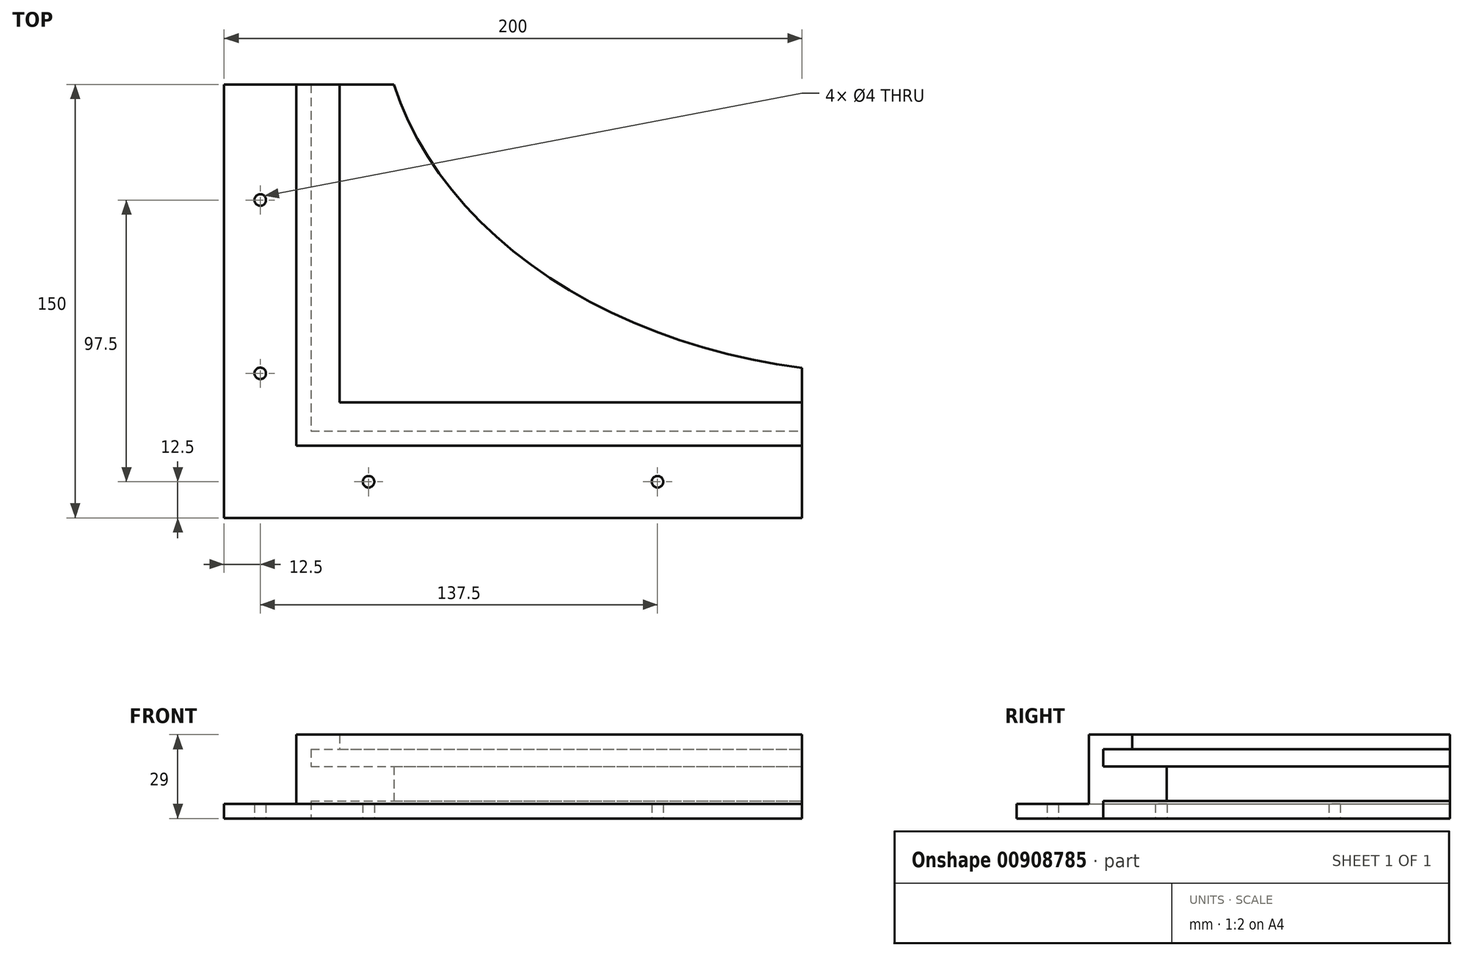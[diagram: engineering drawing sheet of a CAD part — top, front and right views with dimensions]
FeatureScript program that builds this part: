
annotation { "Feature Type Name" : "Feature", "Feature Type Description" : "" }
export const myFeature = defineFeature(function(context is Context, id is Id, definition is map)
    precondition{}
    {
        {
            var Q0;
            Q0=qCreatedBy(makeId("Top.planeOp"),FACE);
            var sketch = newSketch(context, id + "F0", { "sketchPlane" : qUnion([Q0])});
            skEllipticalArc(sketch, "E0", {});
            skLineSegment(sketch, "E1", {"start": v(-176, 0) * mm, "end": v(-176, -130) * mm});
            skPoint(sketch, "E1.endSnap0", {"position": v(0, -130) * mm});
            skLineSegment(sketch, "E2", {"start": v(-176, -130) * mm, "end": v(0, -130) * mm});
            skLineSegment(sketch, "E3", {"start": v(-176, 0) * mm, "end": v(-200, 0) * mm});
            skLineSegment(sketch, "E4", {"start": v(-200, 0) * mm, "end": v(-200, -150) * mm});
            skLineSegment(sketch, "E5", {"start": v(-200, -150) * mm, "end": v(0, -150) * mm});
            skLineSegment(sketch, "E6", {"start": v(0, -150) * mm, "end": v(0, -130) * mm});
            const initialGuessF0  = {"E0": [0, 0, 1, 0, 0.176, 0.13, 3.141592653589793, 4.71238898038469]};
            skSetInitialGuess(sketch, initialGuessF0);
            skSolve(sketch);
        }
        {
            var Q0;
            Q0 = qSketchRegion(id + "F0", true);
            extrude(context, id + "F1", {"entities" : qUnion([Q0]), "depth" : 12 * mm, "offsetDistance" : 25 * mm});
        }
        {
            var Q0;
            Q0=makeQuery(id+"F1.opExtrude","SWEPT_FACE",FACE,{"disambiguationData":[OSD([sQuery(id+"F0.wireOp",EDGE,"E5")])]});
            var sketch = newSketch(context, id + "F2", { "sketchPlane" : qUnion([Q0])});
            skLineSegment(sketch, "E7.bottom", {"start": v(-200, 18) * mm, "end": v(0, 18) * mm});
            skLineSegment(sketch, "E7.top", {"start": v(-200, -6) * mm, "end": v(0, -6) * mm});
            skLineSegment(sketch, "E7.left", {"start": v(-200, 18) * mm, "end": v(-200, -6) * mm});
            skLineSegment(sketch, "E7.right", {"start": v(0, 18) * mm, "end": v(0, -6) * mm});
            skSolve(sketch);
        }
        {
            var Q0;
            Q0 = qSketchRegion(id + "F2", true);
            extrude(context, id + "F3", {"entities" : qUnion([Q0]), "operationType" : NewBodyOperationType.ADD, "depth" : 5 * mm, "offsetDistance" : 25 * mm});
        }
        {
            var Q0;
            Q0=makeQuery(id+"F3.boolean.opBoolean","MERGE",FACE,{"derivedFrom":[makeQuery(id+"F1.opExtrude","SWEPT_FACE",FACE,{"disambiguationData":[OSD([sQuery(id+"F0.wireOp",EDGE,"E4")])]}),makeQuery(id+"F3.opExtrude","SWEPT_FACE",FACE,{"disambiguationData":[OSD([sQuery(id+"F2.wireOp",EDGE,"E7.left")])]})]});
            var sketch = newSketch(context, id + "F4", { "sketchPlane" : qUnion([Q0])});
            skLineSegment(sketch, "E8.bottom", {"start": v(155, 18) * mm, "end": v(0, 18) * mm});
            skLineSegment(sketch, "E8.top", {"start": v(155, -6) * mm, "end": v(0, -6) * mm});
            skLineSegment(sketch, "E8.left", {"start": v(155, 18) * mm, "end": v(155, -6) * mm});
            skLineSegment(sketch, "E8.right", {"start": v(0, 18) * mm, "end": v(0, -6) * mm});
            skSolve(sketch);
        }
        {
            var Q0;
            Q0 = qSketchRegion(id + "F4", true);
            extrude(context, id + "F5", {"entities" : qUnion([Q0]), "operationType" : NewBodyOperationType.ADD, "depth" : 5 * mm, "offsetDistance" : 25 * mm});
        }
        {
            var Q0;
            Q0=makeQuery(id+"F5.boolean.opBoolean","MERGE",FACE,{"derivedFrom":[makeQuery(id+"F3.opExtrude","SWEPT_FACE",FACE,{"disambiguationData":[OSD([sQuery(id+"F2.wireOp",EDGE,"E7.top")])]}),makeQuery(id+"F5.opExtrude","SWEPT_FACE",FACE,{"disambiguationData":[OSD([sQuery(id+"F4.wireOp",EDGE,"E8.top")])]})]});
            var sketch = newSketch(context, id + "F6", { "sketchPlane" : qUnion([Q0])});
            skLineSegment(sketch, "E9", {"start": v(0, 180) * mm, "end": v(-230, 180) * mm});
            skLineSegment(sketch, "E10", {"start": v(-230, 180) * mm, "end": v(-230, 0) * mm});
            skLineSegment(sketch, "E11", {"start": v(-230, 0) * mm, "end": v(-205, 0) * mm});
            skLineSegment(sketch, "E12", {"start": v(-205, 0) * mm, "end": v(-205, 155) * mm});
            skLineSegment(sketch, "E13", {"start": v(-205, 155) * mm, "end": v(0, 155) * mm});
            skLineSegment(sketch, "E14", {"start": v(0, 155) * mm, "end": v(0, 180) * mm});
            skCircle(sketch, "E15", {"center": v(-217.5, 70) * mm, "radius": 2 * mm});
            skCircle(sketch, "E16", {"center": v(-217.5, 130) * mm, "radius": 2 * mm});
            skCircle(sketch, "E17", {"center": v(-180, 167.5) * mm, "radius": 2 * mm});
            skCircle(sketch, "E18", {"center": v(-80, 167.5) * mm, "radius": 2 * mm});
            skSolve(sketch);
        }
        {
            var Q0;
            Q0 = qSketchRegion(id + "F6", true);
            extrude(context, id + "F7", {"entities" : qUnion([Q0]), "operationType" : NewBodyOperationType.ADD, "oppositeDirection" : true, "depth" : 5 * mm, "offsetDistance" : 25 * mm});
        }
        {
            var Q0;
            Q0=makeQuery(id+"F5.boolean.opBoolean","MERGE",FACE,{"derivedFrom":[makeQuery(id+"F3.opExtrude","SWEPT_FACE",FACE,{"disambiguationData":[OSD([sQuery(id+"F2.wireOp",EDGE,"E7.bottom")])]}),makeQuery(id+"F5.opExtrude","SWEPT_FACE",FACE,{"disambiguationData":[OSD([sQuery(id+"F4.wireOp",EDGE,"E8.bottom")])]})]});
            var sketch = newSketch(context, id + "F8", { "sketchPlane" : qUnion([Q0])});
            skLineSegment(sketch, "E19", {"start": v(-205, 0) * mm, "end": v(-190, 0) * mm});
            skLineSegment(sketch, "E20", {"start": v(-190, 0) * mm, "end": v(-190, -140) * mm});
            skLineSegment(sketch, "E21", {"start": v(-190, -140) * mm, "end": v(0, -140) * mm});
            skLineSegment(sketch, "E22", {"start": v(0, -140) * mm, "end": v(0, -155) * mm});
            skLineSegment(sketch, "E23", {"start": v(0, -155) * mm, "end": v(-205, -155) * mm});
            skLineSegment(sketch, "E24", {"start": v(-205, -155) * mm, "end": v(-205, 0) * mm});
            skSolve(sketch);
        }
        {
            var Q0;
            Q0 = qSketchRegion(id + "F8", true);
            extrude(context, id + "F9", {"entities" : qUnion([Q0]), "operationType" : NewBodyOperationType.ADD, "depth" : 5 * mm, "offsetDistance" : 25 * mm});
        }
        {
            var Q0;
            Q0=qCreatedBy(makeId("Top.planeOp"),FACE);
            var sketch = newSketch(context, id + "F10", { "sketchPlane" : qUnion([Q0])});
            skLineSegment(sketch, "E25.bottom", {"start": v(-230, 0) * mm, "end": v(0, 0) * mm});
            skLineSegment(sketch, "E25.top", {"start": v(-230, -30) * mm, "end": v(0, -30) * mm});
            skLineSegment(sketch, "E25.left", {"start": v(-230, 0) * mm, "end": v(-230, -30) * mm});
            skLineSegment(sketch, "E25.right", {"start": v(0, 0) * mm, "end": v(0, -30) * mm});
            skLineSegment(sketch, "E26.bottom", {"start": v(0, -180) * mm, "end": v(-30, -180) * mm});
            skLineSegment(sketch, "E26.top", {"start": v(0, 0) * mm, "end": v(-30, 0) * mm});
            skLineSegment(sketch, "E26.left", {"start": v(0, -180) * mm, "end": v(0, 0) * mm});
            skLineSegment(sketch, "E26.right", {"start": v(-30, -180) * mm, "end": v(-30, 0) * mm});
            skSolve(sketch);
        }
        {
            var Q0;
            Q0 = qSketchRegion(id + "F10", true);
            extrude(context, id + "F11", {"entities" : qUnion([Q0]), "operationType" : NewBodyOperationType.REMOVE, "endBound" : BoundingType.SYMMETRIC, "oppositeDirection" : true, "depth" : 50 * mm, "offsetDistance" : 25 * mm});
        }
    });
